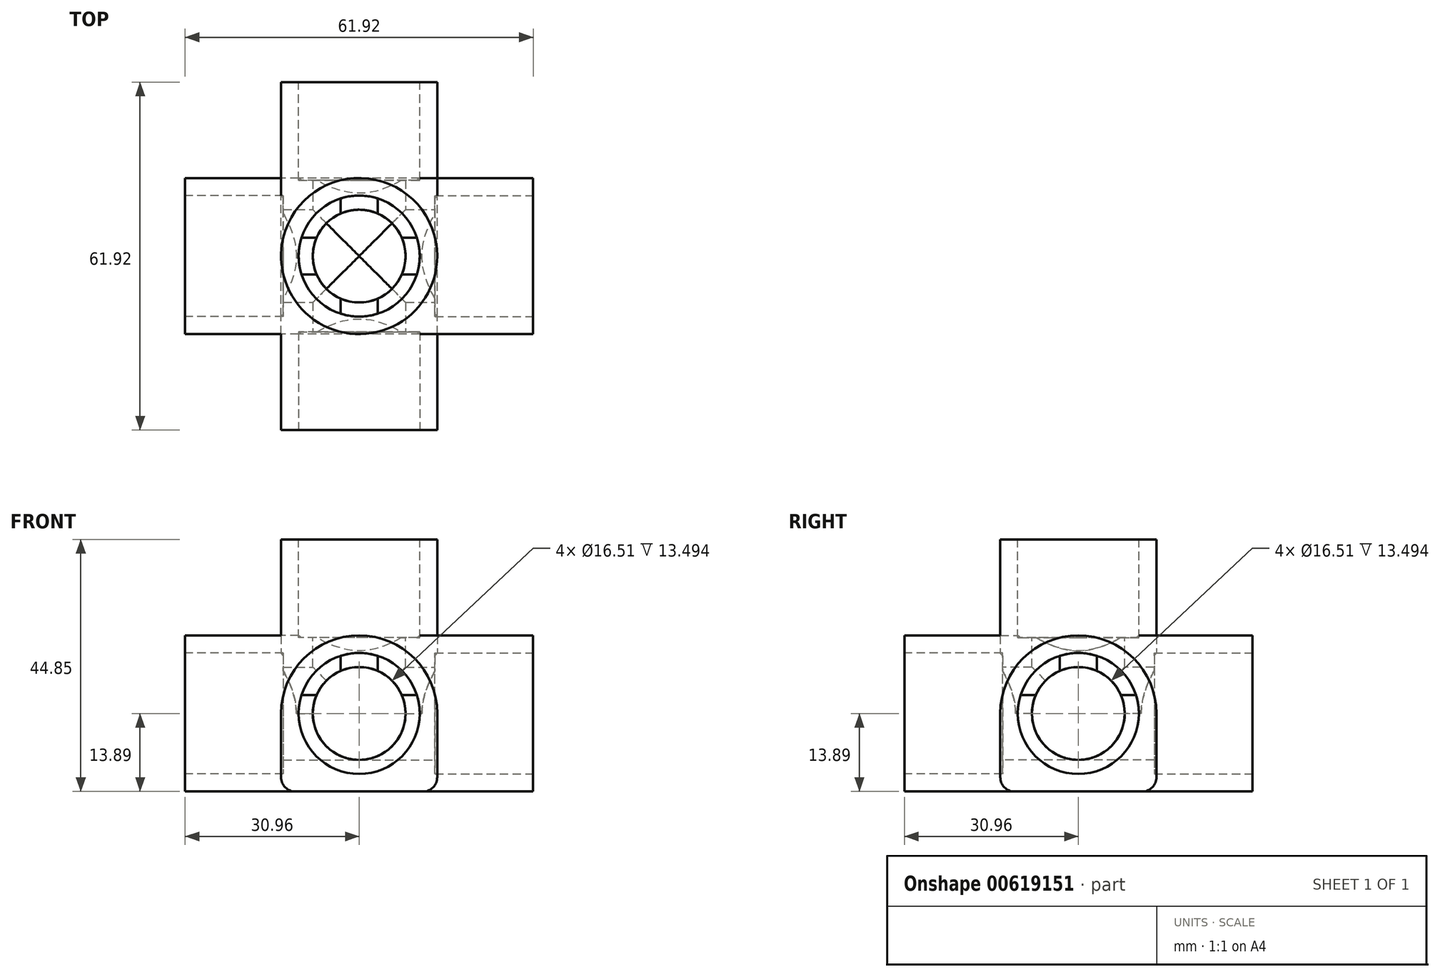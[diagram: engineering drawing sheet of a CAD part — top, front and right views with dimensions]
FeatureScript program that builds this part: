
annotation { "Feature Type Name" : "Feature", "Feature Type Description" : "" }
export const myFeature = defineFeature(function(context is Context, id is Id, definition is map)
    precondition{}
    {
        {
            var Q0;
            Q0=qCreatedBy(makeId("Front.planeOp"),FACE);
            var sketch = newSketch(context, id + "F0", { "sketchPlane" : qUnion([Q0])});
            skArc(sketch, "E0", {"start": v(13.9, 0) * mm, "mid": v(0, 13.9) * mm, "end": v(-13.9, 0) * mm});
            skLineSegment(sketch, "E1.top", {"start": v(-11.35, -13.9) * mm, "end": v(11.35, -13.9) * mm});
            skLineSegment(sketch, "E1.left", {"start": v(-13.9, 0) * mm, "end": v(-13.9, -11.35) * mm});
            skLineSegment(sketch, "E1.right", {"start": v(13.9, 0) * mm, "end": v(13.9, -11.35) * mm});
            skPoint(sketch, "E2.visualSharp", {"position": v(-13.9, -13.9) * mm});
            skArc(sketch, "E2.filletArc", {"start": v(-13.9, -11.35) * mm, "mid": v(-13.15, -13.15) * mm, "end": v(-11.35, -13.9) * mm});
            skPoint(sketch, "E3.visualSharp", {"position": v(13.9, -13.9) * mm});
            skArc(sketch, "E3.filletArc", {"start": v(11.35, -13.9) * mm, "mid": v(13.15, -13.15) * mm, "end": v(13.9, -11.35) * mm});
            skSolve(sketch);
        }
        {
            var Q0;
            Q0=makeQuery(id+"F0.imprint","IMPRINT",FACE,{"disambiguationData":[TD([[makeQuery(id+"F0.imprint","IMPRINT",EDGE,{"derivedFrom":sQuery(id+"F0.wireOp",EDGE,"E0")}),1.0]])]});
            extrude(context, id + "F1", {"entities" : qUnion([Q0]), "depth" : 30.96 * mm, "offsetDistance" : 25.4 * mm, "hasSecondDirection" : true, "secondDirectionOppositeDirection" : true, "secondDirectionDepth" : 30.96 * mm});
        }
        {
            var Q0;
            Q0=qCreatedBy(makeId("Right.planeOp"),FACE);
            var sketch = newSketch(context, id + "F2", { "sketchPlane" : qUnion([Q0])});
            skArc(sketch, "E4", {"start": v(13.9, 0) * mm, "mid": v(0, 13.9) * mm, "end": v(-13.9, 0) * mm});
            skLineSegment(sketch, "E5.top", {"start": v(-11.35, -13.9) * mm, "end": v(11.35, -13.9) * mm});
            skLineSegment(sketch, "E5.left", {"start": v(-13.9, 0) * mm, "end": v(-13.9, -11.35) * mm});
            skLineSegment(sketch, "E5.right", {"start": v(13.9, 0) * mm, "end": v(13.9, -11.35) * mm});
            skPoint(sketch, "E6.visualSharp", {"position": v(-13.9, -13.9) * mm});
            skArc(sketch, "E6.filletArc", {"start": v(-13.9, -11.35) * mm, "mid": v(-13.15, -13.15) * mm, "end": v(-11.35, -13.9) * mm});
            skPoint(sketch, "E7.visualSharp", {"position": v(13.9, -13.9) * mm});
            skArc(sketch, "E7.filletArc", {"start": v(11.35, -13.9) * mm, "mid": v(13.15, -13.15) * mm, "end": v(13.9, -11.35) * mm});
            skSolve(sketch);
        }
        {
            var Q0;
            Q0 = qSketchRegion(id + "F2", true);
            extrude(context, id + "F3", {"entities" : qUnion([Q0]), "depth" : 30.96 * mm, "offsetDistance" : 25.4 * mm, "hasSecondDirection" : true, "secondDirectionOppositeDirection" : true, "secondDirectionDepth" : 30.96 * mm});
        }
        {
            var Q0;
            Q0=qCreatedBy(makeId("Top.planeOp"),FACE);
            var sketch = newSketch(context, id + "F4", { "sketchPlane" : qUnion([Q0])});
            skCircle(sketch, "E8", {"center": v(0, 0) * mm, "radius": 13.9 * mm});
            skSolve(sketch);
        }
        {
            var Q0;
            Q0 = qSketchRegion(id + "F4", true);
            extrude(context, id + "F5", {"entities" : qUnion([Q0]), "depth" : 30.96 * mm, "offsetDistance" : 25.4 * mm});
        }
        {
            var Q0;
            Q0=makeQuery(id+"F1.opExtrude","CAP_FACE",FACE,{"disambiguationData":[OSD([sQuery(id+"F0.wireOp",EDGE,"E0"),sQuery(id+"F0.wireOp",EDGE,"E1.top"),sQuery(id+"F0.wireOp",EDGE,"E1.left"),sQuery(id+"F0.wireOp",EDGE,"E1.right"),sQuery(id+"F0.wireOp",EDGE,"E2.filletArc"),sQuery(id+"F0.wireOp",EDGE,"E3.filletArc")])],"isStart":true});
            var sketch = newSketch(context, id + "F6", { "sketchPlane" : qUnion([Q0])});
            skCircle(sketch, "E9", {"center": v(0, 0) * mm, "radius": 10.77 * mm});
            skSolve(sketch);
        }
        {
            var Q0;
            Q0 = qSketchRegion(id + "F6", true);
            extrude(context, id + "F7", {"entities" : qUnion([Q0]), "operationType" : NewBodyOperationType.REMOVE, "oppositeDirection" : true, "depth" : 17.46 * mm, "offsetDistance" : 25.4 * mm});
        }
        {
            var Q0;
            Q0=makeQuery(id+"F3.opExtrude","CAP_FACE",FACE,{"disambiguationData":[OSD([sQuery(id+"F2.wireOp",EDGE,"E4"),sQuery(id+"F2.wireOp",EDGE,"E5.top"),sQuery(id+"F2.wireOp",EDGE,"E5.left"),sQuery(id+"F2.wireOp",EDGE,"E5.right"),sQuery(id+"F2.wireOp",EDGE,"E6.filletArc"),sQuery(id+"F2.wireOp",EDGE,"E7.filletArc")])],"isStart":true});
            var sketch = newSketch(context, id + "F8", { "sketchPlane" : qUnion([Q0])});
            skCircle(sketch, "E10", {"center": v(0, 0) * mm, "radius": 10.77 * mm});
            skSolve(sketch);
        }
        {
            var Q0;
            Q0=makeQuery(id+"F1.opExtrude","CAP_FACE",FACE,{"disambiguationData":[OSD([sQuery(id+"F0.wireOp",EDGE,"E0"),sQuery(id+"F0.wireOp",EDGE,"E1.top"),sQuery(id+"F0.wireOp",EDGE,"E1.left"),sQuery(id+"F0.wireOp",EDGE,"E1.right"),sQuery(id+"F0.wireOp",EDGE,"E2.filletArc"),sQuery(id+"F0.wireOp",EDGE,"E3.filletArc")])],"isStart":false});
            var sketch = newSketch(context, id + "F9", { "sketchPlane" : qUnion([Q0])});
            skCircle(sketch, "E11", {"center": v(0, 0) * mm, "radius": 10.77 * mm});
            skSolve(sketch);
        }
        {
            var Q0;
            Q0=makeQuery(id+"F5.opExtrude","CAP_FACE",FACE,{"disambiguationData":[OSD([sQuery(id+"F4.wireOp",EDGE,"E8")])],"isStart":false});
            var sketch = newSketch(context, id + "F10", { "sketchPlane" : qUnion([Q0])});
            skCircle(sketch, "E12", {"center": v(0, 0) * mm, "radius": 10.77 * mm});
            skSolve(sketch);
        }
        {
            var Q0;
            Q0=makeQuery(id+"F3.opExtrude","CAP_FACE",FACE,{"disambiguationData":[OSD([sQuery(id+"F2.wireOp",EDGE,"E4"),sQuery(id+"F2.wireOp",EDGE,"E5.top"),sQuery(id+"F2.wireOp",EDGE,"E5.left"),sQuery(id+"F2.wireOp",EDGE,"E5.right"),sQuery(id+"F2.wireOp",EDGE,"E6.filletArc"),sQuery(id+"F2.wireOp",EDGE,"E7.filletArc")])],"isStart":false});
            var sketch = newSketch(context, id + "F11", { "sketchPlane" : qUnion([Q0])});
            skCircle(sketch, "E13", {"center": v(0, 0) * mm, "radius": 10.77 * mm});
            skSolve(sketch);
        }
        {
            var Q0;
            Q0 = qSketchRegion(id + "F11", true);
            extrude(context, id + "F12", {"entities" : qUnion([Q0]), "operationType" : NewBodyOperationType.REMOVE, "oppositeDirection" : true, "depth" : 17.46 * mm, "offsetDistance" : 25.4 * mm});
        }
        {
            var Q0;
            Q0 = qSketchRegion(id + "F10", true);
            extrude(context, id + "F13", {"entities" : qUnion([Q0]), "operationType" : NewBodyOperationType.REMOVE, "oppositeDirection" : true, "depth" : 17.46 * mm, "offsetDistance" : 25.4 * mm});
        }
        {
            var Q0;
            Q0 = qSketchRegion(id + "F9", true);
            extrude(context, id + "F14", {"entities" : qUnion([Q0]), "operationType" : NewBodyOperationType.REMOVE, "oppositeDirection" : true, "depth" : 17.46 * mm, "offsetDistance" : 25.4 * mm});
        }
        {
            var Q0;
            Q0 = qSketchRegion(id + "F8", true);
            extrude(context, id + "F15", {"entities" : qUnion([Q0]), "operationType" : NewBodyOperationType.REMOVE, "oppositeDirection" : true, "depth" : 17.46 * mm, "offsetDistance" : 25.4 * mm});
        }
        {
            var Q0;
            Q0=makeQuery(id+"F1.opExtrude","CAP_FACE",FACE,{"disambiguationData":[OSD([sQuery(id+"F0.wireOp",EDGE,"E0"),sQuery(id+"F0.wireOp",EDGE,"E1.top"),sQuery(id+"F0.wireOp",EDGE,"E1.left"),sQuery(id+"F0.wireOp",EDGE,"E1.right"),sQuery(id+"F0.wireOp",EDGE,"E2.filletArc"),sQuery(id+"F0.wireOp",EDGE,"E3.filletArc")])],"isStart":false});
            var sketch = newSketch(context, id + "F16", { "sketchPlane" : qUnion([Q0])});
            skCircle(sketch, "E14", {"center": v(0, 0) * mm, "radius": 8.26 * mm});
            skSolve(sketch);
        }
        {
            var Q0;
            Q0 = qSketchRegion(id + "F16", true);
            extrude(context, id + "F17", {"entities" : qUnion([Q0]), "operationType" : NewBodyOperationType.REMOVE, "endBound" : BoundingType.THROUGH_ALL, "oppositeDirection" : true, "depth" : 25.4 * mm, "offsetDistance" : 25.4 * mm});
        }
        {
            var Q0;
            Q0=makeQuery(id+"F3.opExtrude","CAP_FACE",FACE,{"disambiguationData":[OSD([sQuery(id+"F2.wireOp",EDGE,"E4"),sQuery(id+"F2.wireOp",EDGE,"E5.top"),sQuery(id+"F2.wireOp",EDGE,"E5.left"),sQuery(id+"F2.wireOp",EDGE,"E5.right"),sQuery(id+"F2.wireOp",EDGE,"E6.filletArc"),sQuery(id+"F2.wireOp",EDGE,"E7.filletArc")])],"isStart":false});
            var sketch = newSketch(context, id + "F18", { "sketchPlane" : qUnion([Q0])});
            skCircle(sketch, "E15", {"center": v(0, 0) * mm, "radius": 8.26 * mm});
            skSolve(sketch);
        }
        {
            var Q0;
            Q0 = qSketchRegion(id + "F18", true);
            extrude(context, id + "F19", {"entities" : qUnion([Q0]), "operationType" : NewBodyOperationType.REMOVE, "endBound" : BoundingType.THROUGH_ALL, "oppositeDirection" : true, "depth" : 25.4 * mm, "offsetDistance" : 25.4 * mm});
        }
        {
            var Q0;
            Q0=makeQuery(id+"F5.opExtrude","CAP_FACE",FACE,{"disambiguationData":[OSD([sQuery(id+"F4.wireOp",EDGE,"E8")])],"isStart":false});
            var sketch = newSketch(context, id + "F20", { "sketchPlane" : qUnion([Q0])});
            skCircle(sketch, "E16", {"center": v(0, 0) * mm, "radius": 8.26 * mm});
            skSolve(sketch);
        }
        {
            var Q0;
            Q0 = qSketchRegion(id + "F20", true);
            var Q1;
            {var subQ0=makeQuery(id+"F19.opExtrude","SWEPT_FACE",FACE,{"disambiguationData":[OSD([sQuery(id+"F18.wireOp",EDGE,"E15")])]});Q1=makeQuery(id+"F19.boolean.opBoolean","COPY",FACE,{"disambiguationData":[TD([makeQuery(id+"F12.boolean.opBoolean","COPY",FACE,{"derivedFrom":makeQuery(id+"F12.opExtrude","CAP_FACE",FACE,{"disambiguationData":[OSD([sQuery(id+"F11.wireOp",EDGE,"E13")])],"isStart":false})}),makeQuery(id+"F17.boolean.opBoolean","COPY",FACE,{"disambiguationData":[TD([makeQuery(id+"F3.opExtrude","SWEPT_FACE",FACE,{"disambiguationData":[OSD([sQuery(id+"F2.wireOp",EDGE,"E4")])]})])],"derivedFrom":makeQuery(id+"F17.opExtrude","SWEPT_FACE",FACE,{"disambiguationData":[OSD([sQuery(id+"F16.wireOp",EDGE,"E14")])]})}),subQ0])],"derivedFrom":subQ0});}
            extrude(context, id + "F21", {"entities" : qUnion([Q0]), "operationType" : NewBodyOperationType.REMOVE, "endBound" : BoundingType.UP_TO_SURFACE, "oppositeDirection" : true, "depth" : 25.4 * mm, "endBoundEntityFace" : qUnion([Q1]), "offsetDistance" : 25.4 * mm});
        }
    });
